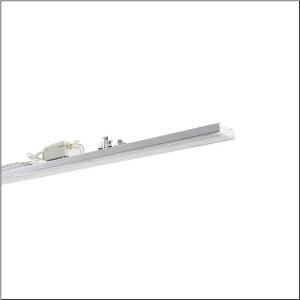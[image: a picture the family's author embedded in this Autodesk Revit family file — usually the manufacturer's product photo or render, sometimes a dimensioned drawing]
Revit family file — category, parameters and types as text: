
# Revit family: licross_r__21_recessed_mo_52tl11dv4fxg_3abc
name_source: partatom
category: Lighting Fixtures
units: mm (PartAtom-declared; Revit-internal decimal feet)

## family parameters
Cut with Voids When Loaded = No
Host = Face
Light Source = No
Part Type = Normal
Room Calculation Point = No
Round Connector Dimension = Use Diameter
Shared = No

## types (1)
- --- (1 x LED, 15180 lm, 85.3 W, 4000K)
    Apparent Load = 85 VA
    CIE Flux Codes = 89 96 99 100 100
    Color Rendering = 80
    Color Temperature = 4000K
    Default Elevation = 1800 mm
    Description = Licross® 21 Recessed MO, luminaire insert, of sheet steel, galvanised, coil coated, white, length: 2.250mm, width: 66mm, height: 67mm, LED rated luminous flux: 15.180lm, light colour: 840, control gear: DALI 2, with plug, 5-pole, with phase selection, mains connection: 220..240V, AC, 50/60Hz, rated input power: 85W, halogen-free wiring, primary light control with lens, of plastic, primary optical cover: cover, of PMMA, light emission: direct distribution, primary light characteristic: symmetric, protection rating (complete): IP40, insulation class (complete): insulation class I (protective earthing), certification: CE, ENEC, VDE, UKCA, protection symbol: D if used in an environment without relevant dust loads with corresponding accessories, impact resistance: IK06, permissible ambient temperature for indoor applications: -25..+35°C, corresponds to IFS (International Featured Standards) requirements for safety and quality in the food industry, reducing of maximum allowable ambient temperature of 5°C with ceiling mounting, LABS conformity tested according to VDMA 24364:2018-05, packaging unit: 1 piece
    Height = 58 mm
    Lamp = 1 x LED
    Lamp Light Flux = 15180 lm
    Lamp Power = 85.3 W
    Lamp count = 1
    Length = 2250 mm
    Luminous efficacy = 178 lm/W
    Manufacturer = Siteco
    ModVariant = No
    Model = 52TL11DV4FXG
    Mounting Place = Ceiling
    Mounting Type = Pendant
    Number of Poles = 1
    OnlyDefault = Yes
    Power Factor = 1
    Product Name = Licross® 21 Recessed MO
    Product group = luminaire insert
    ProductGroupID = 901
    Protection Class = Protection class I
    Protection Degree = IP 40
    RLX_Detail_Level = 1
    RLX_Emergency_Light_Flux = 0 lm
    RLX_Emergency_Type = 0
    RLX_Emergency_Type_DB = No
    RlxData = <blob elided: 29405 chars, md5=6f886a6b>
    Socket = socket
    Standby Power = 0 W
    System Light Flux = 15180 lm
    System Power = 85 W
    Type Comments = factory setting: luminous flux: 100 % | dim-lin: 254 | 390 mA
    Type Image = l_1296930.jpg
    URL = http://relux.com
    VarID = @adj_058703
    Voltage = 0 V
    Weight = 0.00 kg
    Width = 66 mm

## geometry (parser evidence)
native form markers: Blend x4, Sweep x8
no freeform markers — native parametric forms only
